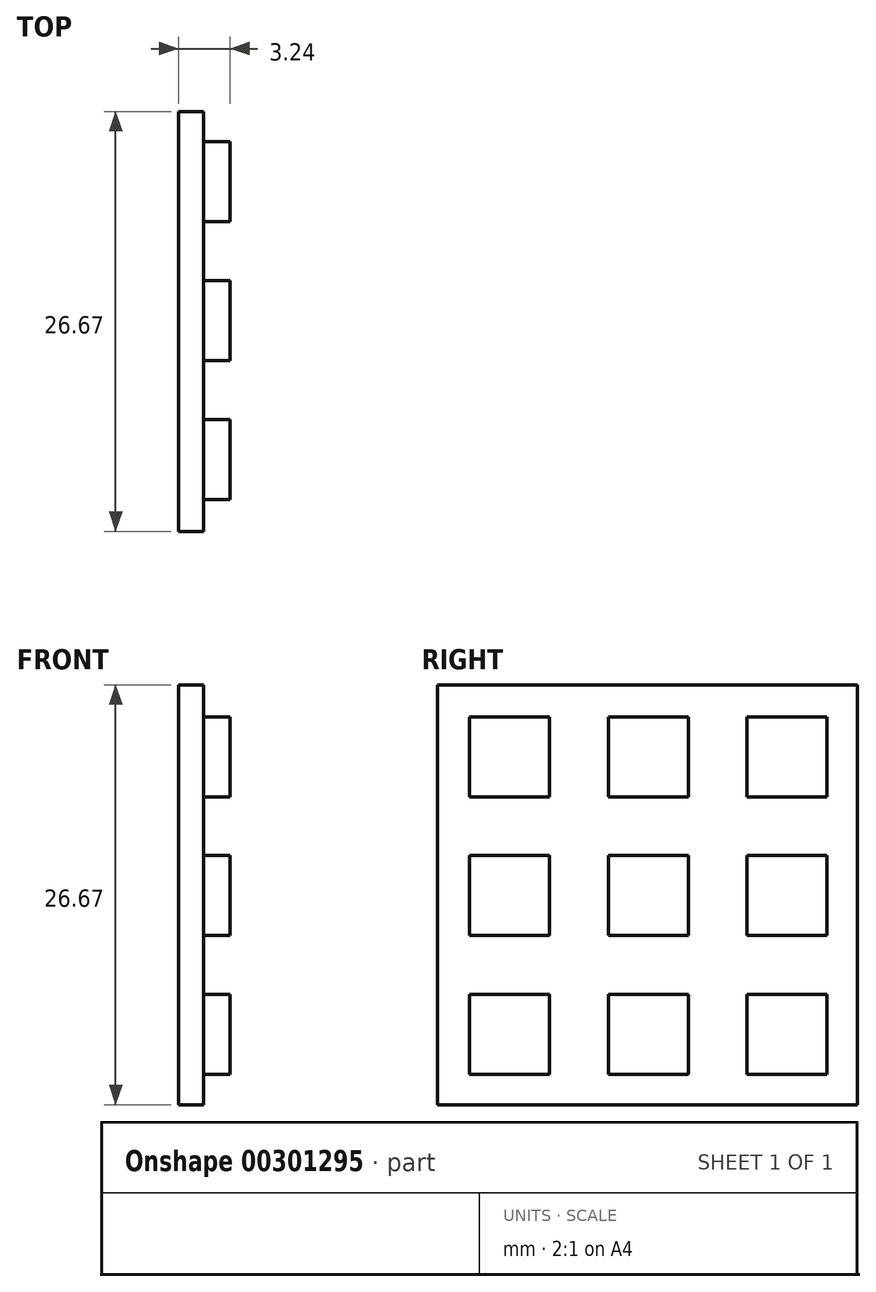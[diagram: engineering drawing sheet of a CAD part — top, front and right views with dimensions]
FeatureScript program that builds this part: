
annotation { "Feature Type Name" : "Feature", "Feature Type Description" : "" }
export const myFeature = defineFeature(function(context is Context, id is Id, definition is map)
    precondition{}
    {
        {
            var Q0;
            Q0=qCreatedBy(makeId("Right.planeOp"),FACE);
            var sketch = newSketch(context, id + "F0", { "sketchPlane" : qUnion([Q0])});
            skLineSegment(sketch, "E0.bottom", {"start": v(0, 0) * mm, "end": v(26.67, 0) * mm});
            skLineSegment(sketch, "E0.top", {"start": v(0, 26.67) * mm, "end": v(26.67, 26.67) * mm});
            skLineSegment(sketch, "E0.left", {"start": v(0, 0) * mm, "end": v(0, 26.67) * mm});
            skLineSegment(sketch, "E0.right", {"start": v(26.67, 0) * mm, "end": v(26.67, 26.67) * mm});
            skSolve(sketch);
        }
        {
            var Q0;
            Q0 = qSketchRegion(id + "F0", true);
            extrude(context, id + "F1", {"entities" : qUnion([Q0]), "depth" : 1.59 * mm});
        }
        {
            var Q0;
            Q0=makeQuery(id+"F1.opExtrude","CAP_FACE",FACE,{"disambiguationData":[OSD([sQuery(id+"F0.wireOp",EDGE,"E0.bottom"),sQuery(id+"F0.wireOp",EDGE,"E0.top"),sQuery(id+"F0.wireOp",EDGE,"E0.left"),sQuery(id+"F0.wireOp",EDGE,"E0.right")])],"isStart":false});
            var sketch = newSketch(context, id + "F2", { "sketchPlane" : qUnion([Q0])});
            skLineSegment(sketch, "E1.bottom", {"start": v(2.03, 24.64) * mm, "end": v(7.11, 24.64) * mm});
            skLineSegment(sketch, "E1.top", {"start": v(2.03, 19.56) * mm, "end": v(7.11, 19.56) * mm});
            skLineSegment(sketch, "E1.left", {"start": v(2.03, 24.64) * mm, "end": v(2.03, 19.56) * mm});
            skLineSegment(sketch, "E1.right", {"start": v(7.11, 24.64) * mm, "end": v(7.11, 19.56) * mm});
            skLineSegment(sketch, "E2.0.1.0", {"start": v(2.03, 15.82) * mm, "end": v(7.11, 15.82) * mm});
            skLineSegment(sketch, "E2.0.1.1", {"start": v(2.03, 10.74) * mm, "end": v(7.11, 10.74) * mm});
            skLineSegment(sketch, "E2.0.1.2", {"start": v(2.03, 15.82) * mm, "end": v(2.03, 10.74) * mm});
            skLineSegment(sketch, "E2.0.1.3", {"start": v(7.11, 15.82) * mm, "end": v(7.11, 10.74) * mm});
            skLineSegment(sketch, "E2.0.2.0", {"start": v(2.03, 7.01) * mm, "end": v(7.11, 7.01) * mm});
            skLineSegment(sketch, "E2.0.2.1", {"start": v(2.03, 1.93) * mm, "end": v(7.11, 1.93) * mm});
            skLineSegment(sketch, "E2.0.2.2", {"start": v(2.03, 7.01) * mm, "end": v(2.03, 1.93) * mm});
            skLineSegment(sketch, "E2.0.2.3", {"start": v(7.11, 7.01) * mm, "end": v(7.11, 1.93) * mm});
            skLineSegment(sketch, "E2.1.0.0", {"start": v(10.85, 24.64) * mm, "end": v(15.93, 24.64) * mm});
            skLineSegment(sketch, "E2.1.0.1", {"start": v(10.85, 19.56) * mm, "end": v(15.93, 19.56) * mm});
            skLineSegment(sketch, "E2.1.0.2", {"start": v(10.85, 24.64) * mm, "end": v(10.85, 19.56) * mm});
            skLineSegment(sketch, "E2.1.0.3", {"start": v(15.93, 24.64) * mm, "end": v(15.93, 19.56) * mm});
            skLineSegment(sketch, "E2.1.1.0", {"start": v(10.85, 15.82) * mm, "end": v(15.93, 15.82) * mm});
            skLineSegment(sketch, "E2.1.1.1", {"start": v(10.85, 10.74) * mm, "end": v(15.93, 10.74) * mm});
            skLineSegment(sketch, "E2.1.1.2", {"start": v(10.85, 15.82) * mm, "end": v(10.85, 10.74) * mm});
            skLineSegment(sketch, "E2.1.1.3", {"start": v(15.93, 15.82) * mm, "end": v(15.93, 10.74) * mm});
            skLineSegment(sketch, "E2.1.2.0", {"start": v(10.85, 7.01) * mm, "end": v(15.93, 7.01) * mm});
            skLineSegment(sketch, "E2.1.2.1", {"start": v(10.85, 1.93) * mm, "end": v(15.93, 1.93) * mm});
            skLineSegment(sketch, "E2.1.2.2", {"start": v(10.85, 7.01) * mm, "end": v(10.85, 1.93) * mm});
            skLineSegment(sketch, "E2.1.2.3", {"start": v(15.93, 7.01) * mm, "end": v(15.93, 1.93) * mm});
            skLineSegment(sketch, "E2.2.0.0", {"start": v(19.66, 24.64) * mm, "end": v(24.74, 24.64) * mm});
            skLineSegment(sketch, "E2.2.0.1", {"start": v(19.66, 19.56) * mm, "end": v(24.74, 19.56) * mm});
            skLineSegment(sketch, "E2.2.0.2", {"start": v(19.66, 24.64) * mm, "end": v(19.66, 19.56) * mm});
            skLineSegment(sketch, "E2.2.0.3", {"start": v(24.74, 24.64) * mm, "end": v(24.74, 19.56) * mm});
            skLineSegment(sketch, "E2.2.1.0", {"start": v(19.66, 15.82) * mm, "end": v(24.74, 15.82) * mm});
            skLineSegment(sketch, "E2.2.1.1", {"start": v(19.66, 10.74) * mm, "end": v(24.74, 10.74) * mm});
            skLineSegment(sketch, "E2.2.1.2", {"start": v(19.66, 15.82) * mm, "end": v(19.66, 10.74) * mm});
            skLineSegment(sketch, "E2.2.1.3", {"start": v(24.74, 15.82) * mm, "end": v(24.74, 10.74) * mm});
            skLineSegment(sketch, "E2.2.2.0", {"start": v(19.66, 7.01) * mm, "end": v(24.74, 7.01) * mm});
            skLineSegment(sketch, "E2.2.2.1", {"start": v(19.66, 1.93) * mm, "end": v(24.74, 1.93) * mm});
            skLineSegment(sketch, "E2.2.2.2", {"start": v(19.66, 7.01) * mm, "end": v(19.66, 1.93) * mm});
            skLineSegment(sketch, "E2.2.2.3", {"start": v(24.74, 7.01) * mm, "end": v(24.74, 1.93) * mm});
            skLineSegment(sketch, "E2.direction1", {"start": v(2.03, 19.56) * mm, "end": v(10.85, 19.56) * mm, "construction": true});
            skLineSegment(sketch, "E2.direction2", {"start": v(2.03, 19.56) * mm, "end": v(2.03, 10.74) * mm, "construction": true});
            skSolve(sketch);
        }
        {
            var Q0;
            Q0 = qSketchRegion(id + "F2", true);
            extrude(context, id + "F3", {"entities" : qUnion([Q0]), "operationType" : NewBodyOperationType.ADD, "depth" : 1.65 * mm});
        }
    });
